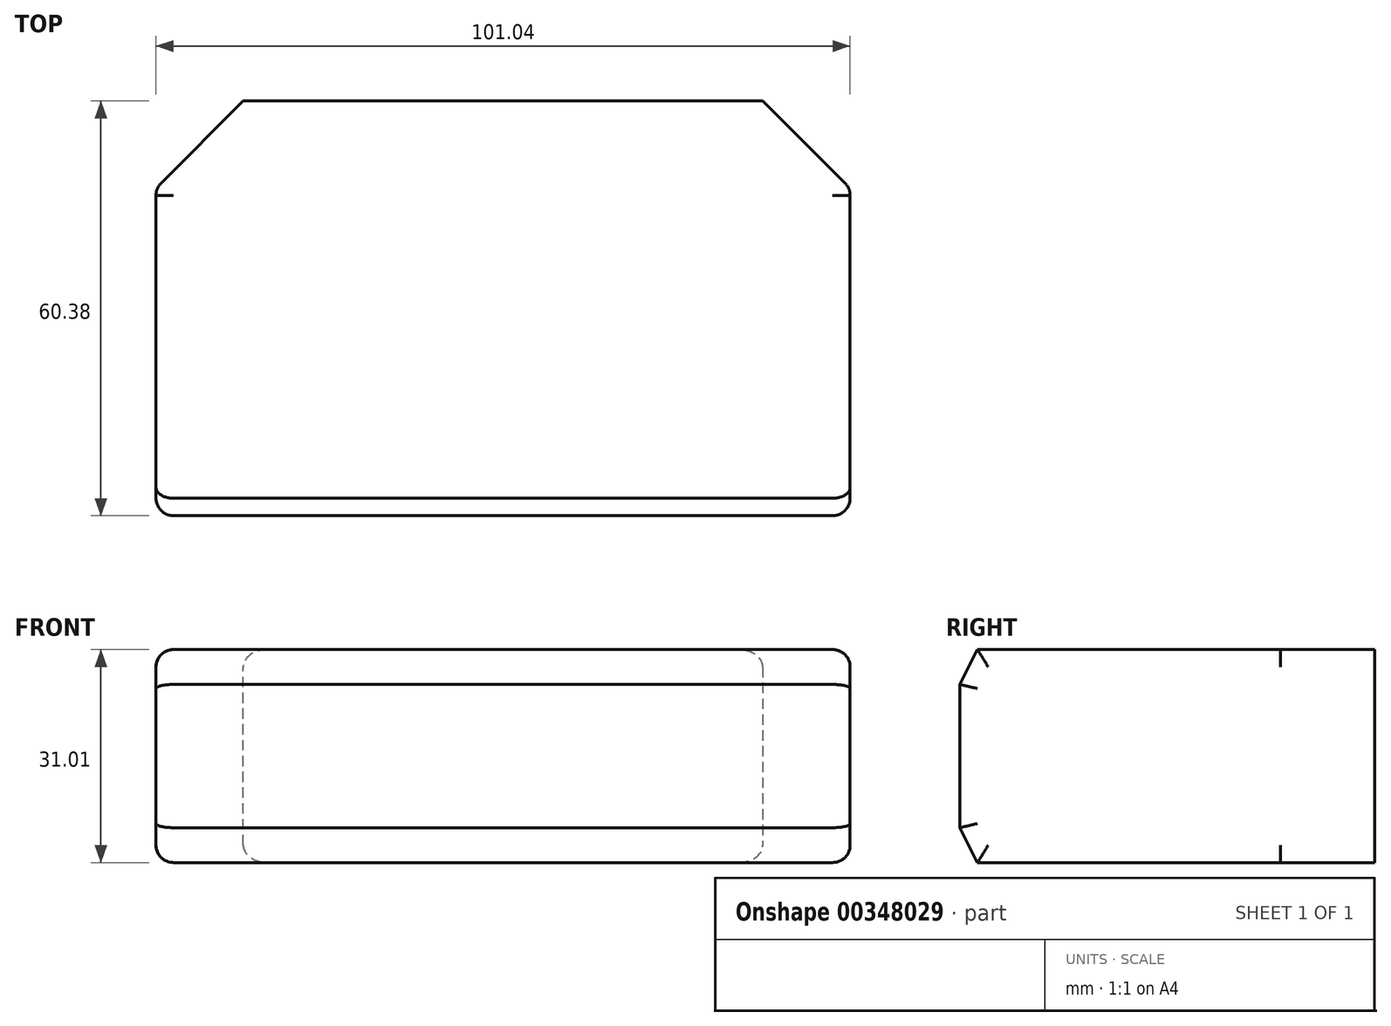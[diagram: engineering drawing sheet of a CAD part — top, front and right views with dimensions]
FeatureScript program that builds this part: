
annotation { "Feature Type Name" : "Feature", "Feature Type Description" : "" }
export const myFeature = defineFeature(function(context is Context, id is Id, definition is map)
    precondition{}
    {
        {
            var Q0;
            Q0=qCreatedBy(makeId("Top.planeOp"),FACE);
            var sketch = newSketch(context, id + "F0", { "sketchPlane" : qUnion([Q0])});
            skLineSegment(sketch, "E0.bottom", {"start": v(50.52, 30.19) * mm, "end": v(-50.52, 30.19) * mm});
            skLineSegment(sketch, "E0.top", {"start": v(50.52, -30.19) * mm, "end": v(-50.52, -30.19) * mm});
            skLineSegment(sketch, "E0.left", {"start": v(50.52, 30.19) * mm, "end": v(50.52, -30.19) * mm});
            skLineSegment(sketch, "E0.right", {"start": v(-50.52, 30.19) * mm, "end": v(-50.52, -30.19) * mm});
            skPoint(sketch, "E0.middle", {"position": v(0, 0) * mm});
            skSolve(sketch);
        }
        {
            var Q0;
            Q0=qSketchRegion(id+"F0",true);
            extrude(context, id + "F1", {"entities" : qUnion([Q0]), "depth" : 31.01 * mm});
        }
        {
            var Q0;
            Q0=makeQuery(id+"F1.opExtrude","SWEPT_FACE",FACE,{"disambiguationData":[OSD([sQuery(id+"F0.wireOp",EDGE,"E0.top")])]});
            var sketch = newSketch(context, id + "F2", { "sketchPlane" : qUnion([Q0])});
            skSolve(sketch);
        }
        {
            var Q0;
            Q0=makeQuery(id+"F1.opExtrude","CAP_EDGE",EDGE,{"disambiguationData":[OSD([sQuery(id+"F0.wireOp",EDGE,"E0.top")])],"isStart":false});
            var Q1;
            Q1=makeQuery(id+"F1.opExtrude","CAP_EDGE",EDGE,{"disambiguationData":[OSD([sQuery(id+"F0.wireOp",EDGE,"E0.top")])],"isStart":true});
            chamfer(context, id + "F3", {"entities" : qUnion([Q0, Q1]), "chamferType" : ChamferType.TWO_OFFSETS, "width1" : 5.08 * mm, "oppositeDirection" : false, "width2" : 2.54 * mm, "tangentPropagation" : true});
        }
        {
            var Q0;
            Q0=makeQuery(id+"F1.opExtrude","SWEPT_EDGE",EDGE,{"disambiguationData":[OSD([sQuery(id+"F0.wireOp",EDGE,"E0.bottom"),sQuery(id+"F0.wireOp",EDGE,"E0.left")])]});
            var Q1;
            Q1=makeQuery(id+"F1.opExtrude","SWEPT_EDGE",EDGE,{"disambiguationData":[OSD([sQuery(id+"F0.wireOp",EDGE,"E0.bottom"),sQuery(id+"F0.wireOp",EDGE,"E0.right")])]});
            chamfer(context, id + "F4", {"entities" : qUnion([Q0, Q1]), "width" : 12.7 * mm, "tangentPropagation" : true});
        }
        {
            var Q0;
            Q0=makeQuery(id+"F1.opExtrude","SWEPT_EDGE",EDGE,{"disambiguationData":[OSD([sQuery(id+"F0.wireOp",EDGE,"E0.top"),sQuery(id+"F0.wireOp",EDGE,"E0.left")])]});
            var Q1;
            Q1=makeQuery(id+"F3.opChamfer","BLEND_EDGE",EDGE,{"blendedFrom":[makeQuery(id+"F1.opExtrude","CAP_EDGE",EDGE,{"disambiguationData":[OSD([sQuery(id+"F0.wireOp",EDGE,"E0.top")])],"isStart":false}),makeQuery(id+"F1.opExtrude","SWEPT_FACE",FACE,{"disambiguationData":[OSD([sQuery(id+"F0.wireOp",EDGE,"E0.left")])]})],"blendedInto":[makeQuery(id+"F1.opExtrude","SWEPT_FACE",FACE,{"disambiguationData":[OSD([sQuery(id+"F0.wireOp",EDGE,"E0.left")])]})]});
            var Q2;
            Q2=makeQuery(id+"F1.opExtrude","CAP_EDGE",EDGE,{"disambiguationData":[OSD([sQuery(id+"F0.wireOp",EDGE,"E0.left")])],"isStart":false});
            var Q3;
            Q3=makeQuery(id+"F1.opExtrude","CAP_EDGE",EDGE,{"disambiguationData":[OSD([sQuery(id+"F0.wireOp",EDGE,"E0.left")])],"isStart":true});
            var Q4;
            Q4=makeQuery(id+"F3.opChamfer","BLEND_EDGE",EDGE,{"blendedFrom":[makeQuery(id+"F1.opExtrude","CAP_EDGE",EDGE,{"disambiguationData":[OSD([sQuery(id+"F0.wireOp",EDGE,"E0.top")])],"isStart":true}),makeQuery(id+"F1.opExtrude","SWEPT_FACE",FACE,{"disambiguationData":[OSD([sQuery(id+"F0.wireOp",EDGE,"E0.left")])]})],"blendedInto":[makeQuery(id+"F1.opExtrude","SWEPT_FACE",FACE,{"disambiguationData":[OSD([sQuery(id+"F0.wireOp",EDGE,"E0.left")])]})]});
            var Q5;
            Q5=makeQuery(id+"F1.opExtrude","CAP_EDGE",EDGE,{"disambiguationData":[OSD([sQuery(id+"F0.wireOp",EDGE,"E0.right")])],"isStart":false});
            var Q6;
            Q6=makeQuery(id+"F1.opExtrude","SWEPT_EDGE",EDGE,{"disambiguationData":[OSD([sQuery(id+"F0.wireOp",EDGE,"E0.top"),sQuery(id+"F0.wireOp",EDGE,"E0.right")])]});
            var Q7;
            Q7=makeQuery(id+"F3.opChamfer","BLEND_EDGE",EDGE,{"blendedFrom":[makeQuery(id+"F1.opExtrude","CAP_EDGE",EDGE,{"disambiguationData":[OSD([sQuery(id+"F0.wireOp",EDGE,"E0.top")])],"isStart":false}),makeQuery(id+"F1.opExtrude","SWEPT_FACE",FACE,{"disambiguationData":[OSD([sQuery(id+"F0.wireOp",EDGE,"E0.right")])]})],"blendedInto":[makeQuery(id+"F1.opExtrude","SWEPT_FACE",FACE,{"disambiguationData":[OSD([sQuery(id+"F0.wireOp",EDGE,"E0.right")])]})]});
            var Q8;
            Q8=makeQuery(id+"F3.opChamfer","BLEND_EDGE",EDGE,{"blendedFrom":[makeQuery(id+"F1.opExtrude","CAP_EDGE",EDGE,{"disambiguationData":[OSD([sQuery(id+"F0.wireOp",EDGE,"E0.top")])],"isStart":true}),makeQuery(id+"F1.opExtrude","SWEPT_FACE",FACE,{"disambiguationData":[OSD([sQuery(id+"F0.wireOp",EDGE,"E0.right")])]})],"blendedInto":[makeQuery(id+"F1.opExtrude","SWEPT_FACE",FACE,{"disambiguationData":[OSD([sQuery(id+"F0.wireOp",EDGE,"E0.right")])]})]});
            var Q9;
            Q9=makeQuery(id+"F1.opExtrude","CAP_EDGE",EDGE,{"disambiguationData":[OSD([sQuery(id+"F0.wireOp",EDGE,"E0.right")])],"isStart":true});
            fillet(context, id + "F5", {"entities" : qUnion([Q0, Q1, Q2, Q3, Q4, Q5, Q6, Q7, Q8, Q9]), "radius" : 2.54 * mm, "tangentPropagation" : true, "allowEdgeOverflow" : false});
        }
        {
            var Q0;
            {var subQ0=sQuery(id+"F0.wireOp",EDGE,"E0.left");var subQ1=sQuery(id+"F0.wireOp",EDGE,"E0.bottom");Q0=makeQuery(id+"F4.opChamfer","BLEND_EDGE",EDGE,{"blendedFrom":[makeQuery(id+"F1.opExtrude","SWEPT_EDGE",EDGE,{"disambiguationData":[OSD([subQ1,subQ0])]}),makeQuery(id+"F1.opExtrude","CAP_FACE",FACE,{"disambiguationData":[OSD([subQ1,sQuery(id+"F0.wireOp",EDGE,"E0.top"),subQ0,sQuery(id+"F0.wireOp",EDGE,"E0.right")])],"isStart":false})],"blendedInto":[makeQuery(id+"F1.opExtrude","CAP_FACE",FACE,{"disambiguationData":[OSD([subQ1,sQuery(id+"F0.wireOp",EDGE,"E0.top"),subQ0,sQuery(id+"F0.wireOp",EDGE,"E0.right")])],"isStart":false})]});}
            var Q1;
            {var subQ0=sQuery(id+"F0.wireOp",EDGE,"E0.left");var subQ1=sQuery(id+"F0.wireOp",EDGE,"E0.bottom");Q1=makeQuery(id+"F4.opChamfer","BLEND_EDGE",EDGE,{"blendedFrom":[makeQuery(id+"F1.opExtrude","SWEPT_EDGE",EDGE,{"disambiguationData":[OSD([subQ1,subQ0])]}),makeQuery(id+"F1.opExtrude","CAP_FACE",FACE,{"disambiguationData":[OSD([subQ1,sQuery(id+"F0.wireOp",EDGE,"E0.top"),subQ0,sQuery(id+"F0.wireOp",EDGE,"E0.right")])],"isStart":true})],"blendedInto":[makeQuery(id+"F1.opExtrude","CAP_FACE",FACE,{"disambiguationData":[OSD([subQ1,sQuery(id+"F0.wireOp",EDGE,"E0.top"),subQ0,sQuery(id+"F0.wireOp",EDGE,"E0.right")])],"isStart":true})]});}
            var Q2;
            {var subQ0=sQuery(id+"F0.wireOp",EDGE,"E0.right");var subQ1=sQuery(id+"F0.wireOp",EDGE,"E0.bottom");Q2=makeQuery(id+"F4.opChamfer","BLEND_EDGE",EDGE,{"blendedFrom":[makeQuery(id+"F1.opExtrude","SWEPT_EDGE",EDGE,{"disambiguationData":[OSD([subQ1,subQ0])]}),makeQuery(id+"F1.opExtrude","CAP_FACE",FACE,{"disambiguationData":[OSD([subQ1,sQuery(id+"F0.wireOp",EDGE,"E0.top"),sQuery(id+"F0.wireOp",EDGE,"E0.left"),subQ0])],"isStart":false})],"blendedInto":[makeQuery(id+"F1.opExtrude","CAP_FACE",FACE,{"disambiguationData":[OSD([subQ1,sQuery(id+"F0.wireOp",EDGE,"E0.top"),sQuery(id+"F0.wireOp",EDGE,"E0.left"),subQ0])],"isStart":false})]});}
            var Q3;
            {var subQ0=sQuery(id+"F0.wireOp",EDGE,"E0.right");var subQ1=sQuery(id+"F0.wireOp",EDGE,"E0.bottom");Q3=makeQuery(id+"F4.opChamfer","BLEND_EDGE",EDGE,{"blendedFrom":[makeQuery(id+"F1.opExtrude","SWEPT_EDGE",EDGE,{"disambiguationData":[OSD([subQ1,subQ0])]}),makeQuery(id+"F1.opExtrude","CAP_FACE",FACE,{"disambiguationData":[OSD([subQ1,sQuery(id+"F0.wireOp",EDGE,"E0.top"),sQuery(id+"F0.wireOp",EDGE,"E0.left"),subQ0])],"isStart":true})],"blendedInto":[makeQuery(id+"F1.opExtrude","CAP_FACE",FACE,{"disambiguationData":[OSD([subQ1,sQuery(id+"F0.wireOp",EDGE,"E0.top"),sQuery(id+"F0.wireOp",EDGE,"E0.left"),subQ0])],"isStart":true})]});}
            fillet(context, id + "F6", {"entities" : qUnion([Q0, Q1, Q2, Q3]), "radius" : 2.54 * mm, "tangentPropagation" : true, "allowEdgeOverflow" : false});
        }
    });
